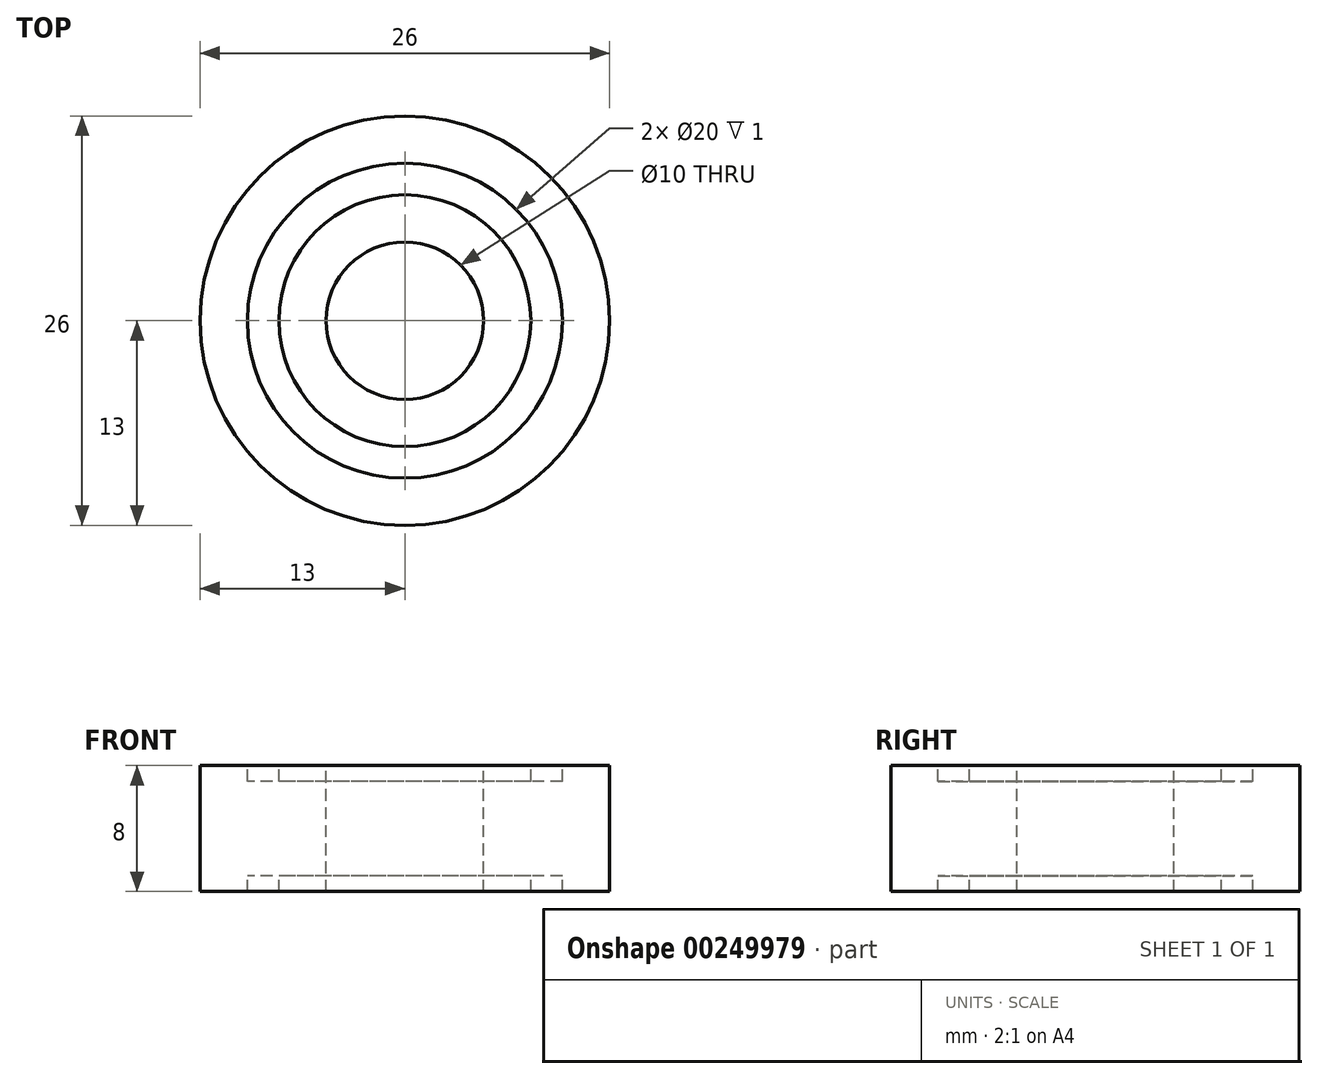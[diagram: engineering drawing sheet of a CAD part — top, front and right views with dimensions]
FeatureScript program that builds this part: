
annotation { "Feature Type Name" : "Feature", "Feature Type Description" : "" }
export const myFeature = defineFeature(function(context is Context, id is Id, definition is map)
    precondition{}
    {
        {
            var Q0;
            Q0=qCreatedBy(makeId("Front.planeOp"),FACE);
            var sketch = newSketch(context, id + "F0", { "sketchPlane" : qUnion([Q0])});
            skLineSegment(sketch, "E0", {"start": v(-13, 4) * mm, "end": v(-13, 0) * mm});
            skLineSegment(sketch, "E1", {"start": v(-13, 4) * mm, "end": v(-10, 4) * mm});
            skLineSegment(sketch, "E2", {"start": v(-5, 4) * mm, "end": v(-5, 0) * mm});
            skLineSegment(sketch, "E3", {"start": v(-10, 4) * mm, "end": v(-10, 3) * mm});
            skLineSegment(sketch, "E4", {"start": v(-8, 4) * mm, "end": v(-8, 3) * mm});
            skLineSegment(sketch, "E5", {"start": v(-10, 3) * mm, "end": v(-8, 3) * mm});
            skLineSegment(sketch, "E6.trimOffspring", {"start": v(-8, 4) * mm, "end": v(-5, 4) * mm});
            skPoint(sketch, "E7", {"position": v(0, 0) * mm});
            skLineSegment(sketch, "E8", {"start": v(0, 16.42) * mm, "end": v(0, -13.94) * mm});
            skLineSegment(sketch, "E9", {"start": v(-18, 0) * mm, "end": v(3.48, 0) * mm, "construction": true});
            skLineSegment(sketch, "E10.MirrorCS", {"start": v(-10, -4) * mm, "end": v(-10, -3) * mm});
            skLineSegment(sketch, "E11.MirrorCS", {"start": v(-8, -4) * mm, "end": v(-8, -3) * mm});
            skLineSegment(sketch, "E12.MirrorCS", {"start": v(-8, -4) * mm, "end": v(-5, -4) * mm});
            skLineSegment(sketch, "E13.MirrorCS", {"start": v(-13, -4) * mm, "end": v(-10, -4) * mm});
            skLineSegment(sketch, "E14.MirrorCS", {"start": v(-13, -4) * mm, "end": v(-13, 0) * mm});
            skLineSegment(sketch, "E15.MirrorCS", {"start": v(-10, -3) * mm, "end": v(-8, -3) * mm});
            skLineSegment(sketch, "E16.MirrorCS", {"start": v(-5, -4) * mm, "end": v(-5, 0) * mm});
            skSolve(sketch);
        }
        {
            var Q0;
            Q0=qSketchRegion(id+"F0",true);
            var Q1;
            Q1=sQuery(id+"F0.wireOp",EDGE,"E8");
            revolve(context, id + "F1", {"entities" : qUnion([Q0]), "axis" : qUnion([Q1]), "revolveType" : RevolveType.FULL});
        }
    });
